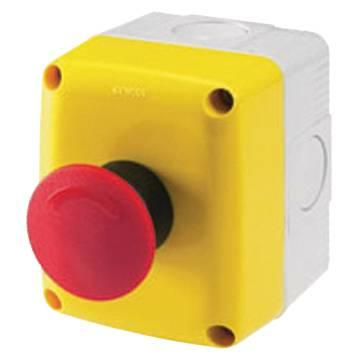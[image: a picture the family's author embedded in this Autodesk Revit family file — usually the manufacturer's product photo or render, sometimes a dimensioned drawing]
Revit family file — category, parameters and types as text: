
# Revit family: Domotics-SerieCivili-GEWISS-27COMBI22-IP66_CONTENITORI_1PULSANTE_D22
name_source: partatom
category: Apparecchi elettrici
revit_build: Autodesk Revit 2016 (Build: 20161004_0715(x64)
units: mm (PartAtom-declared; Revit-internal decimal feet)

## family parameters
Condiviso = No
Host = Muro
Mantenere orientamento annotazione = No
Punto di calcolo locali = No
Quota connettore circolare = Usa diametro
Sempre verticale = Sì
Taglio con vuoti quando caricato = No
Tipo di parte = Normale

## types (1)
- Domotics-SerieCivili-GEWISS-27COMBI22-IP66_CONTENITORI_1PULSANTE_D22
    Altezza = 120 mm  [stored 0.393701 ft]
    Catalogo = DOMOTICS
    Catalogo Serie = 27COMBI
    Classe isolamento = II
    Codice EAN = 8011564055575
    Codice Electrocod = 0212
    Colore = Coperchio giallo
    Contatti = 1 NA-1 NC
    Coppia serraggio viti = 0,8NM
    Descrizione = CONTENITORE 1POS.PULSANTE EMERGENZA
    Dim. esterne BxHxP (mm) = 66x82x65
    Glow Wire Test = 650°C
    Grado di protezione = IP66
    IDF = efe26b69-63c3-467c-94fd-fe2566ba7e56
    IDT = 5a7eeb40-13d5-4b7f-8289-c5ccf35a1a1c
    Immagine tipo = GW27202.jpg
    Larghezza = 80 mm  [stored 0.262467 ft]
    Modello = GW27202
    N. posti = 1
    Norma di riferimento = EN 60947-1 - EN 60947-5-1
    Norma di riferimento: = EN 60947-1 - EN 60947-5-1
    Operatori Ã˜ 22 = Emergenza (rosso)
    Produttore = GEWISS S.p.A.
    Profondità = 65 mm
    Pulsante_1 = Pulsante emergenza - rosso
    SEO = Contenitore
    Scheda Tecnica = https://www.gewiss.com
    Scocca anteriore = Giallo
    Temperatura di installazione = -25 +60 °C
    Termopressione con biglia = 70 °C
    Tipo sfondabili = Asportabili con utensile
    URL = https://www.gewiss.com
    Versione file RFA = 18.0
    Viti coperchio = Acciaio inox

note: [stored X ft] marks values corroborated as IEEE doubles in the binary element streams (Revit-internal decimal feet)
